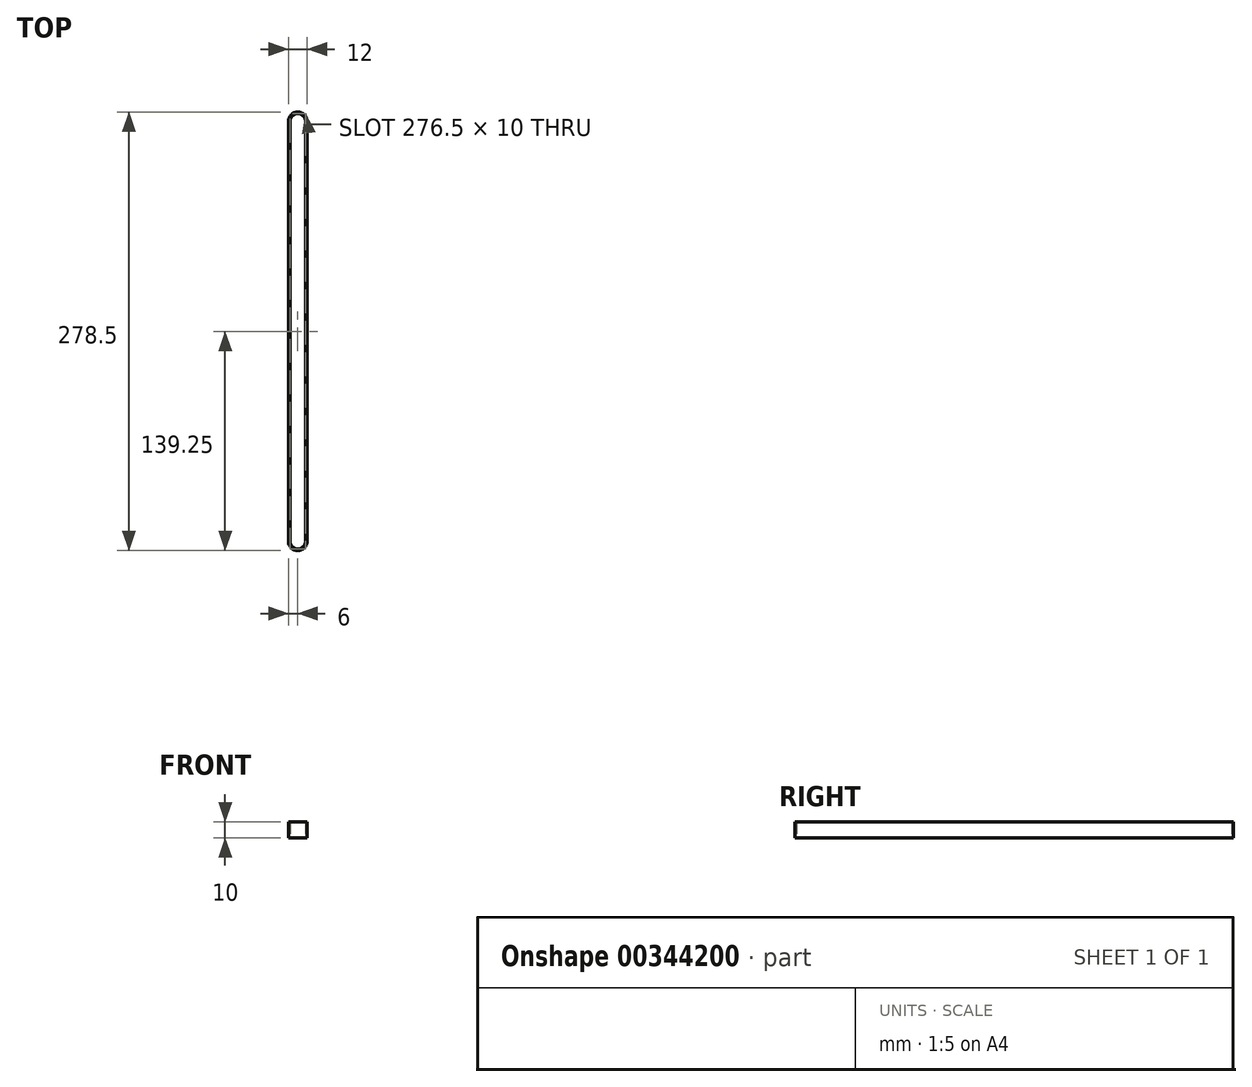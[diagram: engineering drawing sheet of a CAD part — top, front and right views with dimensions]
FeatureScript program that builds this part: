
annotation { "Feature Type Name" : "Feature", "Feature Type Description" : "" }
export const myFeature = defineFeature(function(context is Context, id is Id, definition is map)
    precondition{}
    {
        {
            var Q0;
            Q0=qCreatedBy(makeId("Top.planeOp"),FACE);
            var sketch = newSketch(context, id + "F0", { "sketchPlane" : qUnion([Q0])});
            skArc(sketch, "E0", {"start": v(-5, 0) * mm, "mid": v(0, -5) * mm, "end": v(5, 0) * mm});
            skArc(sketch, "E1", {"start": v(-6, 0) * mm, "mid": v(0, -6) * mm, "end": v(6, 0) * mm});
            skArc(sketch, "E2", {"start": v(5, 266.5) * mm, "mid": v(0, 271.5) * mm, "end": v(-5, 266.5) * mm});
            skArc(sketch, "E3", {"start": v(6, 266.5) * mm, "mid": v(0, 272.5) * mm, "end": v(-6, 266.5) * mm});
            skLineSegment(sketch, "E4", {"start": v(6, 0) * mm, "end": v(6, 266.5) * mm});
            skLineSegment(sketch, "E5", {"start": v(5, 266.5) * mm, "end": v(5, 0) * mm});
            skLineSegment(sketch, "E6", {"start": v(-5, 0) * mm, "end": v(-5, 266.5) * mm});
            skLineSegment(sketch, "E7", {"start": v(-6, 266.5) * mm, "end": v(-6, 0) * mm});
            skSolve(sketch);
        }
        {
            var Q0;
            Q0 = qSketchRegion(id + "F0", true);
            extrude(context, id + "F1", {"entities" : qUnion([Q0]), "depth" : 10 * mm});
        }
    });
